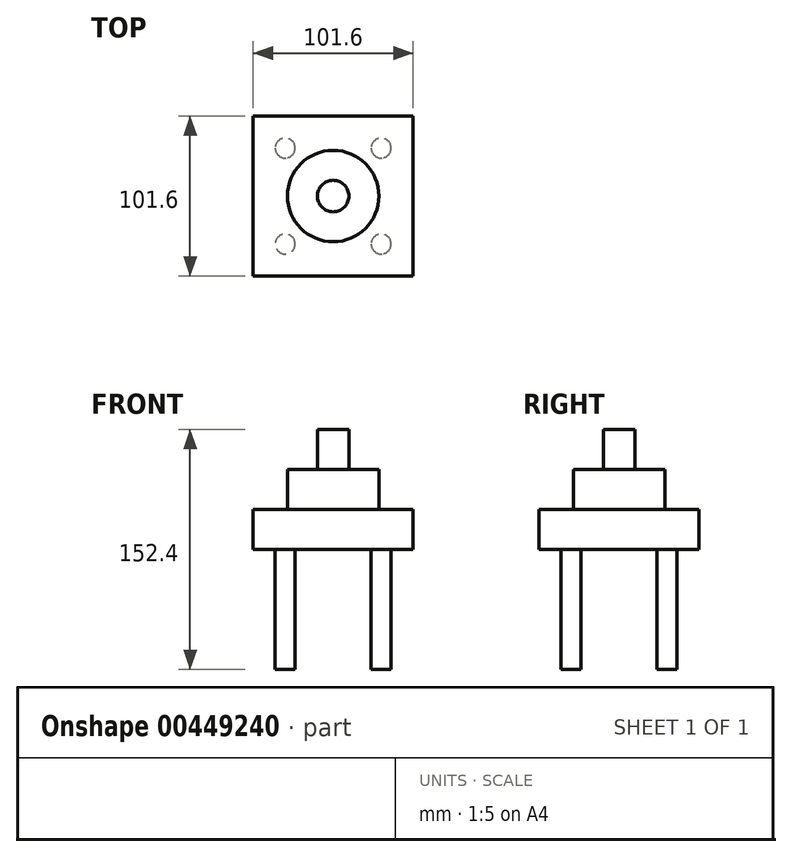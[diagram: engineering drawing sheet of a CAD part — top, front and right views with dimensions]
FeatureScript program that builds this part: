
annotation { "Feature Type Name" : "Feature", "Feature Type Description" : "" }
export const myFeature = defineFeature(function(context is Context, id is Id, definition is map)
    precondition{}
    {
        {
            var Q0;
            Q0=qCreatedBy(makeId("Top.planeOp"),FACE);
            var sketch = newSketch(context, id + "F0", { "sketchPlane" : qUnion([Q0])});
            skLineSegment(sketch, "E0.bottom", {"start": v(50.8, 50.8) * mm, "end": v(-50.8, 50.8) * mm});
            skLineSegment(sketch, "E0.top", {"start": v(50.8, -50.8) * mm, "end": v(-50.8, -50.8) * mm});
            skLineSegment(sketch, "E0.left", {"start": v(50.8, 50.8) * mm, "end": v(50.8, -50.8) * mm});
            skLineSegment(sketch, "E0.right", {"start": v(-50.8, 50.8) * mm, "end": v(-50.8, -50.8) * mm});
            skPoint(sketch, "E0.middle", {"position": v(0, 0) * mm});
            skSolve(sketch);
        }
        {
            var Q0;
            Q0=makeQuery(id+"F0.imprint","IMPRINT",FACE,{"disambiguationData":[TD([[makeQuery(id+"F0.imprint","IMPRINT",EDGE,{"derivedFrom":sQuery(id+"F0.wireOp",EDGE,"E0.bottom")}),1.0]])]});
            extrude(context, id + "F1", {"entities" : qUnion([Q0]), "depth" : 25.4 * mm});
        }
        {
            var Q0;
            Q0=makeQuery(id+"F1.opExtrude","CAP_FACE",FACE,{"disambiguationData":[OSD([sQuery(id+"F0.wireOp",EDGE,"E0.bottom"),sQuery(id+"F0.wireOp",EDGE,"E0.top"),sQuery(id+"F0.wireOp",EDGE,"E0.left"),sQuery(id+"F0.wireOp",EDGE,"E0.right")])],"isStart":false});
            var sketch = newSketch(context, id + "F2", { "sketchPlane" : qUnion([Q0])});
            skCircle(sketch, "E1", {"center": v(0, 0) * mm, "radius": 29.03 * mm});
            skSolve(sketch);
        }
        {
            var Q0;
            Q0=makeQuery(id+"F2.imprint","IMPRINT",FACE,{"disambiguationData":[TD([[makeQuery(id+"F2.imprint","IMPRINT",EDGE,{"derivedFrom":sQuery(id+"F2.wireOp",EDGE,"E1")}),1.0]])]});
            extrude(context, id + "F3", {"entities" : qUnion([Q0]), "operationType" : NewBodyOperationType.ADD, "depth" : 25.4 * mm});
        }
        {
            var Q0;
            Q0=makeQuery(id+"F1.opExtrude","CAP_FACE",FACE,{"disambiguationData":[OSD([sQuery(id+"F0.wireOp",EDGE,"E0.bottom"),sQuery(id+"F0.wireOp",EDGE,"E0.top"),sQuery(id+"F0.wireOp",EDGE,"E0.left"),sQuery(id+"F0.wireOp",EDGE,"E0.right")])],"isStart":true});
            var sketch = newSketch(context, id + "F4", { "sketchPlane" : qUnion([Q0])});
            skCircle(sketch, "E2", {"center": v(-30.48, 30.48) * mm, "radius": 6.35 * mm});
            skCircle(sketch, "E3.1.0", {"center": v(30.48, 30.48) * mm, "radius": 6.35 * mm});
            skCircle(sketch, "E3.2.0", {"center": v(30.48, -30.48) * mm, "radius": 6.35 * mm});
            skCircle(sketch, "E3.3.0", {"center": v(-30.48, -30.48) * mm, "radius": 6.35 * mm});
            skPoint(sketch, "E3.center", {"position": v(0, 0) * mm});
            skLineSegment(sketch, "E3.anchor1", {"start": v(0, 0) * mm, "end": v(-30.48, 30.48) * mm, "construction": true});
            skLineSegment(sketch, "E3.anchor2", {"start": v(0, 0) * mm, "end": v(-30.48, -30.48) * mm, "construction": true});
            skSolve(sketch);
        }
        {
            var Q0;
            Q0 = qSketchRegion(id + "F4", true);
            extrude(context, id + "F5", {"entities" : qUnion([Q0]), "operationType" : NewBodyOperationType.ADD, "depth" : 76.2 * mm});
        }
        {
            var Q0;
            Q0=makeQuery(id+"F3.opExtrude","CAP_FACE",FACE,{"disambiguationData":[OSD([sQuery(id+"F2.wireOp",EDGE,"E1")])],"isStart":false});
            var sketch = newSketch(context, id + "F6", { "sketchPlane" : qUnion([Q0])});
            skCircle(sketch, "E4", {"center": v(0, 0) * mm, "radius": 10 * mm});
            skSolve(sketch);
        }
        {
            var Q0;
            Q0=makeQuery(id+"F6.imprint","IMPRINT",FACE,{"disambiguationData":[TD([[makeQuery(id+"F6.imprint","IMPRINT",EDGE,{"derivedFrom":sQuery(id+"F6.wireOp",EDGE,"E4")}),1.0]])]});
            extrude(context, id + "F7", {"entities" : qUnion([Q0]), "operationType" : NewBodyOperationType.ADD, "depth" : 25.4 * mm});
        }
    });
